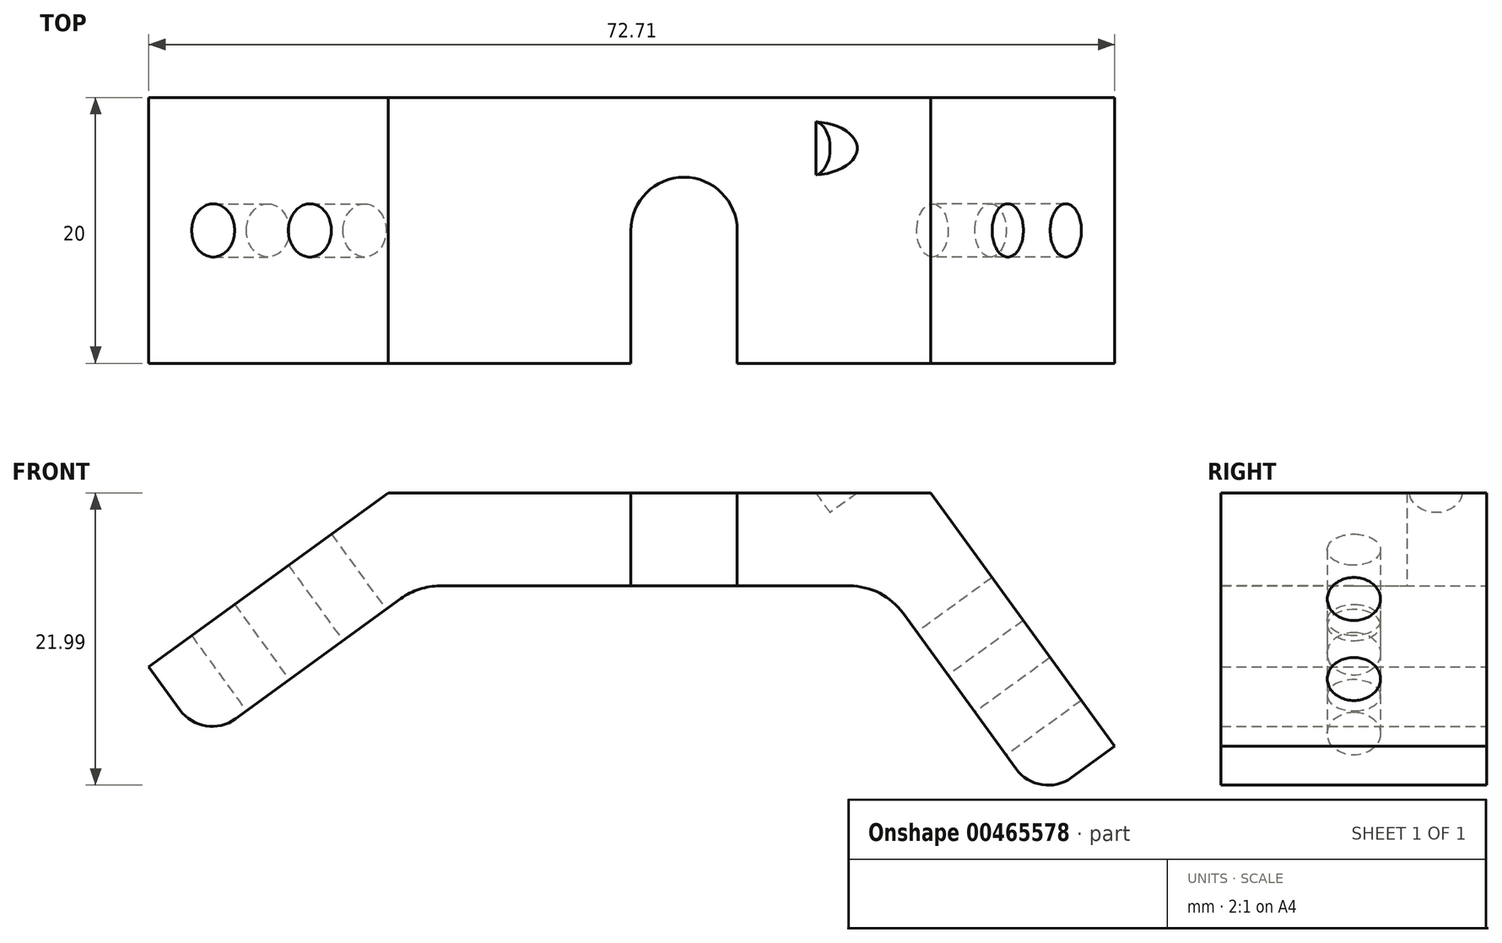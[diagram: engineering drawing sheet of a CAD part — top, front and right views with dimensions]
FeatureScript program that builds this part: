
annotation { "Feature Type Name" : "Feature", "Feature Type Description" : "" }
export const myFeature = defineFeature(function(context is Context, id is Id, definition is map)
    precondition{}
    {
        {
            var Q0;
            Q0=qCreatedBy(makeId("Front.planeOp"),FACE);
            var sketch = newSketch(context, id + "F0", { "sketchPlane" : qUnion([Q0])});
            skLineSegment(sketch, "E0", {"start": v(-36.18, -11.76) * mm, "end": v(-20, 0) * mm});
            skLineSegment(sketch, "E1", {"start": v(-20, 0) * mm, "end": v(15, 0) * mm});
            skLineSegment(sketch, "E2", {"start": v(15, 0) * mm, "end": v(26.76, -16.18) * mm});
            skLineSegment(sketch, "E3.0", {"start": v(18.57, 7) * mm, "end": v(32.42, -12.07) * mm});
            skLineSegment(sketch, "E3.1", {"start": v(-22.27, 7) * mm, "end": v(18.57, 7) * mm});
            skLineSegment(sketch, "E3.2", {"start": v(-40.3, -6.1) * mm, "end": v(-22.27, 7) * mm});
            skLineSegment(sketch, "E4", {"start": v(-40.3, -6.1) * mm, "end": v(-36.18, -11.76) * mm});
            skLineSegment(sketch, "E5", {"start": v(26.76, -16.18) * mm, "end": v(32.42, -12.07) * mm});
            skSolve(sketch);
        }
        {
            var Q0;
            Q0=qSketchRegion(id+"F0",true);
            extrude(context, id + "F1", {"entities" : qUnion([Q0]), "depth" : 10 * mm, "hasSecondDirection" : true, "secondDirectionOppositeDirection" : true, "secondDirectionDepth" : 10 * mm});
        }
        {
            var Q0;
            Q0=makeQuery(id+"F1.opExtrude","SWEPT_FACE",FACE,{"disambiguationData":[OSD([sQuery(id+"F0.wireOp",EDGE,"E0")])]});
            var sketch = newSketch(context, id + "F2", { "sketchPlane" : qUnion([Q0])});
            skPoint(sketch, "E6", {"position": v(0, -37.85) * mm});
            skPoint(sketch, "E7", {"position": v(0, -24) * mm});
            skPoint(sketch, "E8", {"position": v(-30.18, 0) * mm});
            skPoint(sketch, "E9", {"position": v(-21.18, 0) * mm});
            skSolve(sketch);
        }
        {
            var Q0;
            Q0=sQuery(id+"F2.wireOp",VERTEX,"E6");
            var Q1;
            Q1=sQuery(id+"F2.wireOp",VERTEX,"E7");
            var Q2;
            Q2=sQuery(id+"F2.wireOp",VERTEX,"E8");
            var Q3;
            Q3=sQuery(id+"F2.wireOp",VERTEX,"E9");
            var Q4;
            Q4=makeQuery(id+"F1.opExtrude","SWEPT_BODY",BODY,{"disambiguationData":[OSD([sQuery(id+"F0.wireOp",EDGE,"E0"),sQuery(id+"F0.wireOp",EDGE,"E1"),sQuery(id+"F0.wireOp",EDGE,"E2"),sQuery(id+"F0.wireOp",EDGE,"E3.0"),sQuery(id+"F0.wireOp",EDGE,"E3.1"),sQuery(id+"F0.wireOp",EDGE,"E3.2"),sQuery(id+"F0.wireOp",EDGE,"E4"),sQuery(id+"F0.wireOp",EDGE,"E5")])]});
            hole(context, id + "F3", {"style" : HoleStyle.SIMPLE, "endStyle" : HoleEndStyle.THROUGH, "holeDiameter" : 4 * mm, "isTappedThrough" : true, "tappedDepth" : 12 * mm, "tapClearance" : 3, "locations" : qUnion([Q0, Q1, Q2, Q3]), "scope" : qUnion([Q4])});
        }
        {
            var Q0;
            Q0=makeQuery(id+"F1.opExtrude","SWEPT_FACE",FACE,{"disambiguationData":[OSD([sQuery(id+"F0.wireOp",EDGE,"E2")])]});
            var sketch = newSketch(context, id + "F4", { "sketchPlane" : qUnion([Q0])});
            skPoint(sketch, "E10", {"position": v(16.06, 0) * mm});
            skPoint(sketch, "E11", {"position": v(-6.17, 0) * mm});
            skPoint(sketch, "E12", {"position": v(0, -13.82) * mm});
            skPoint(sketch, "E13", {"position": v(0, -22.82) * mm});
            skSolve(sketch);
        }
        {
            var Q0;
            Q0=sQuery(id+"F4.wireOp",VERTEX,"E10");
            var Q1;
            Q1=sQuery(id+"F4.wireOp",VERTEX,"E11");
            var Q2;
            Q2=makeQuery(id+"F1.opExtrude","SWEPT_BODY",BODY,{"disambiguationData":[OSD([sQuery(id+"F0.wireOp",EDGE,"E0"),sQuery(id+"F0.wireOp",EDGE,"E1"),sQuery(id+"F0.wireOp",EDGE,"E2"),sQuery(id+"F0.wireOp",EDGE,"E3.0"),sQuery(id+"F0.wireOp",EDGE,"E3.1"),sQuery(id+"F0.wireOp",EDGE,"E3.2"),sQuery(id+"F0.wireOp",EDGE,"E4"),sQuery(id+"F0.wireOp",EDGE,"E5")])]});
            hole(context, id + "F5", {"style" : HoleStyle.SIMPLE, "endStyle" : HoleEndStyle.THROUGH, "holeDiameter" : 4 * mm, "isTappedThrough" : true, "tappedDepth" : 12 * mm, "tapClearance" : 3, "locations" : qUnion([Q0, Q1]), "scope" : qUnion([Q2])});
        }
        {
            var Q0;
            Q0=makeQuery(id+"F1.opExtrude","SWEPT_FACE",FACE,{"disambiguationData":[OSD([sQuery(id+"F0.wireOp",EDGE,"E1")])]});
            var sketch = newSketch(context, id + "F6", { "sketchPlane" : qUnion([Q0])});
            skPoint(sketch, "E14", {"position": v(0, 0) * mm});
            skSolve(sketch);
        }
        {
            var Q0;
            Q0=sQuery(id+"F6.wireOp",VERTEX,"E14");
            var Q1;
            Q1=makeQuery(id+"F1.opExtrude","SWEPT_BODY",BODY,{"disambiguationData":[OSD([sQuery(id+"F0.wireOp",EDGE,"E0"),sQuery(id+"F0.wireOp",EDGE,"E1"),sQuery(id+"F0.wireOp",EDGE,"E2"),sQuery(id+"F0.wireOp",EDGE,"E3.0"),sQuery(id+"F0.wireOp",EDGE,"E3.1"),sQuery(id+"F0.wireOp",EDGE,"E3.2"),sQuery(id+"F0.wireOp",EDGE,"E4"),sQuery(id+"F0.wireOp",EDGE,"E5")])]});
            hole(context, id + "F7", {"style" : HoleStyle.SIMPLE, "endStyle" : HoleEndStyle.THROUGH, "holeDiameter" : 8 * mm, "isTappedThrough" : true, "tappedDepth" : 12 * mm, "tapClearance" : 3, "locations" : qUnion([Q0]), "scope" : qUnion([Q1])});
        }
        {
            var Q0;
            Q0=makeQuery(id+"F1.opExtrude","SWEPT_EDGE",EDGE,{"disambiguationData":[OSD([sQuery(id+"F0.wireOp",EDGE,"E0"),sQuery(id+"F0.wireOp",EDGE,"E4")])]});
            var Q1;
            Q1=makeQuery(id+"F1.opExtrude","SWEPT_EDGE",EDGE,{"disambiguationData":[OSD([sQuery(id+"F0.wireOp",EDGE,"E2"),sQuery(id+"F0.wireOp",EDGE,"E5")])]});
            fillet(context, id + "F8", {"entities" : qUnion([Q0, Q1]), "radius" : 3 * mm, "tangentPropagation" : true, "allowEdgeOverflow" : false});
        }
        {
            var Q0;
            Q0=makeQuery(id+"F1.opExtrude","SWEPT_EDGE",EDGE,{"disambiguationData":[OSD([sQuery(id+"F0.wireOp",EDGE,"E0"),sQuery(id+"F0.wireOp",EDGE,"E1")])]});
            var Q1;
            Q1=makeQuery(id+"F1.opExtrude","SWEPT_EDGE",EDGE,{"disambiguationData":[OSD([sQuery(id+"F0.wireOp",EDGE,"E1"),sQuery(id+"F0.wireOp",EDGE,"E2")])]});
            fillet(context, id + "F9", {"entities" : qUnion([Q0, Q1]), "radius" : 5 * mm, "tangentPropagation" : true, "allowEdgeOverflow" : false});
        }
        {
            var Q0;
            Q0=makeQuery(id+"F1.opExtrude","SWEPT_FACE",FACE,{"disambiguationData":[OSD([sQuery(id+"F0.wireOp",EDGE,"E2")])]});
            var sketch = newSketch(context, id + "F10", { "sketchPlane" : qUnion([Q0])});
            skPoint(sketch, "E15", {"position": v(0, -15.11) * mm});
            skPoint(sketch, "E16", {"position": v(0, -22.55) * mm});
            skSolve(sketch);
        }
        {
            var Q0;
            Q0=sQuery(id+"F10.wireOp",VERTEX,"E15");
            var Q1;
            Q1=sQuery(id+"F10.wireOp",VERTEX,"E16");
            var Q2;
            Q2=makeQuery(id+"F1.opExtrude","SWEPT_BODY",BODY,{"disambiguationData":[OSD([sQuery(id+"F0.wireOp",EDGE,"E0"),sQuery(id+"F0.wireOp",EDGE,"E1"),sQuery(id+"F0.wireOp",EDGE,"E2"),sQuery(id+"F0.wireOp",EDGE,"E3.0"),sQuery(id+"F0.wireOp",EDGE,"E3.1"),sQuery(id+"F0.wireOp",EDGE,"E3.2"),sQuery(id+"F0.wireOp",EDGE,"E4"),sQuery(id+"F0.wireOp",EDGE,"E5")])]});
            hole(context, id + "F11", {"style" : HoleStyle.SIMPLE, "endStyle" : HoleEndStyle.THROUGH, "holeDiameter" : 4 * mm, "isTappedThrough" : true, "tappedDepth" : 12 * mm, "tapClearance" : 3, "locations" : qUnion([Q0, Q1]), "scope" : qUnion([Q2])});
        }
        {
            var Q0;
            Q0=makeQuery(id+"F1.opExtrude","SWEPT_FACE",FACE,{"disambiguationData":[OSD([sQuery(id+"F0.wireOp",EDGE,"E1")])]});
            var sketch = newSketch(context, id + "F12", { "sketchPlane" : qUnion([Q0])});
            skLineSegment(sketch, "E17", {"start": v(-4, 0) * mm, "end": v(-4, 10) * mm});
            skLineSegment(sketch, "E18", {"start": v(4, 0) * mm, "end": v(4, 10) * mm});
            skSolve(sketch);
        }
        {
            var Q0;
            {var subQ0=sQuery(id+"F12.wireOp",EDGE,"E17");Q0=makeQuery(id+"F12.imprint","IMPRINT",FACE,{"disambiguationData":[TD([[makeQuery(id+"F12.imprint","IMPRINT",EDGE,{"derivedFrom":subQ0}),-1.0]])]});}
            extrude(context, id + "F13", {"entities" : qUnion([Q0]), "operationType" : NewBodyOperationType.REMOVE, "oppositeDirection" : true, "depth" : 25 * mm});
        }
    });
